# Revit family: 511_CP_nailfin
name_source: partatom
category: Windows
revit_build: Autodesk Revit 2016 (Build: 20150220_1215(x64)
units: mm (PartAtom-declared; Revit-internal decimal feet)

## family parameters
Always vertical = Yes
Cut with Voids When Loaded = No
Host = Wall
OmniClass Number = 23.30.20.00
OmniClass Title = Windows
Room Calculation Point = No
Shared = No

## types (64) — shared parameters
Default Sill Height = 31 1/2"
MLW1 = 3 1/4"
MLW2 = 3 5/8"
MLW3 = 2 13/16"
Wall Closure = By host

## per-type parameters (varying)
| type | Bar set | Height | MLH | MLW4 | Width |
| 48x36 | 24" | 36" | 18" | 4 1/2" | 48" |
| 72x48 | 36" | 48" | 24" | 6" | 72" |
| 25.5x19.75Min | 13 1/2" | 19 3/4" | 9 7/8" | 2 1/2" | 25 1/2" |
| 96x72Max | 30" | 72" | 36" | 9" | 96" |
| 36x24 | 18" | 24" | 12" | 3" | 36" |
| 60x48 | 30" | 48" | 24" | 6" | 60" |
| 30x24 | 18" | 24" | 12" | 3" | 30" |
| 30x30 | 18" | 30" | 15" | 3 3/4" | 30" |
| 30x36 | 18" | 36" | 18" | 4 1/2" | 30" |
| 30x42 | 18" | 42" | 21" | 5 1/4" | 30" |
| 30x48 | 18" | 48" | 24" | 6" | 30" |
| 30x54 | 18" | 54" | 27" | 6 3/4" | 30" |
| 36x30 | 18" | 30" | 15" | 3 3/4" | 36" |
| 36x36 | 18" | 36" | 18" | 4 1/2" | 36" |
| 36x42 | 18" | 42" | 21" | 5 1/4" | 36" |
| 36x48 | 18" | 48" | 24" | 6" | 36" |
| 36x54 | 18" | 54" | 27" | 6 3/4" | 36" |
| 42x24 | 24" | 24" | 12" | 3" | 42" |
| 42x30 | 24" | 30" | 15" | 3 3/4" | 42" |
| 42x36 | 24" | 36" | 18" | 4 1/2" | 42" |
| 42x42 | 24" | 42" | 21" | 5 1/4" | 42" |
| 42x48 | 24" | 48" | 24" | 6" | 42" |
| 42x54 | 24" | 54" | 27" | 6 3/4" | 42" |
| 42x60 | 24" | 60" | 30" | 7 1/2" | 42" |
| 48x30 | 24" | 30" | 15" | 3 3/4" | 48" |
| 48x42 | 24" | 42" | 21" | 5 1/4" | 48" |
| 48x48 | 24" | 48" | 24" | 6" | 48" |
| 48x54 | 24" | 54" | 27" | 6 3/4" | 48" |
| 48x60 | 24" | 60" | 30" | 7 1/2" | 48" |
| 48x66 | 24" | 66" | 33" | 8 1/4" | 48" |
| 54x30 | 30" | 30" | 15" | 3 3/4" | 54" |
| 54x36 | 30" | 36" | 18" | 4 1/2" | 54" |
| 54x42 | 30" | 42" | 21" | 5 1/4" | 54" |
| 54x48 | 30" | 48" | 24" | 6" | 54" |
| 54x54 | 30" | 54" | 27" | 6 3/4" | 54" |
| 54x60 | 30" | 60" | 30" | 7 1/2" | 54" |
| 54x66 | 30" | 66" | 33" | 8 1/4" | 54" |
| 54x72 | 30" | 72" | 36" | 9" | 54" |
| 60x36 | 30" | 36" | 18" | 4 1/2" | 60" |
| 60x42 | 30" | 42" | 21" | 5 1/4" | 60" |
| 60x54 | 30" | 54" | 27" | 6 3/4" | 60" |
| 60x60 | 30" | 60" | 30" | 7 1/2" | 60" |
| 60x66 | 30" | 66" | 33" | 8 1/4" | 60" |
| 60x72 | 30" | 72" | 36" | 9" | 60" |
| 66x36 | 30" | 36" | 18" | 4 1/2" | 66" |
| 66x42 | 30" | 42" | 21" | 5 1/4" | 66" |
| 66x48 | 30" | 48" | 24" | 6" | 66" |
| 66x54 | 30" | 54" | 27" | 6 3/4" | 66" |
| 66x60 | 30" | 60" | 30" | 7 1/2" | 66" |
| 66x66 | 30" | 66" | 33" | 8 1/4" | 66" |
| 66x72 | 30" | 66" | 33" | 8 1/4" | 66" |
| 72x54 | 36" | 54" | 27" | 6 3/4" | 72" |
| 72x60 | 36" | 60" | 30" | 7 1/2" | 72" |
| 72x66 | 30" | 66" | 33" | 8 1/4" | 72" |
| 72x72 | 30" | 72" | 36" | 9" | 72" |
| 90x54 | 36" | 54" | 27" | 6 3/4" | 90" |
| 90x48 | 36" | 48" | 24" | 6" | 90" |
| 90x60 | 36" | 60" | 30" | 7 1/2" | 90" |
| 90x66 | 30" | 66" | 33" | 8 1/4" | 90" |
| 90x72 | 30" | 72" | 36" | 9" | 90" |
| 96x48 | 36" | 48" | 24" | 6" | 96" |
| 96x54 | 36" | 54" | 27" | 6 3/4" | 96" |
| 96x60 | 36" | 60" | 30" | 7 1/2" | 96" |
| 96x66 | 30" | 66" | 33" | 8 1/4" | 96" |

## geometry (parser evidence)
native form markers: Sweep x3
no freeform markers — native parametric forms only
